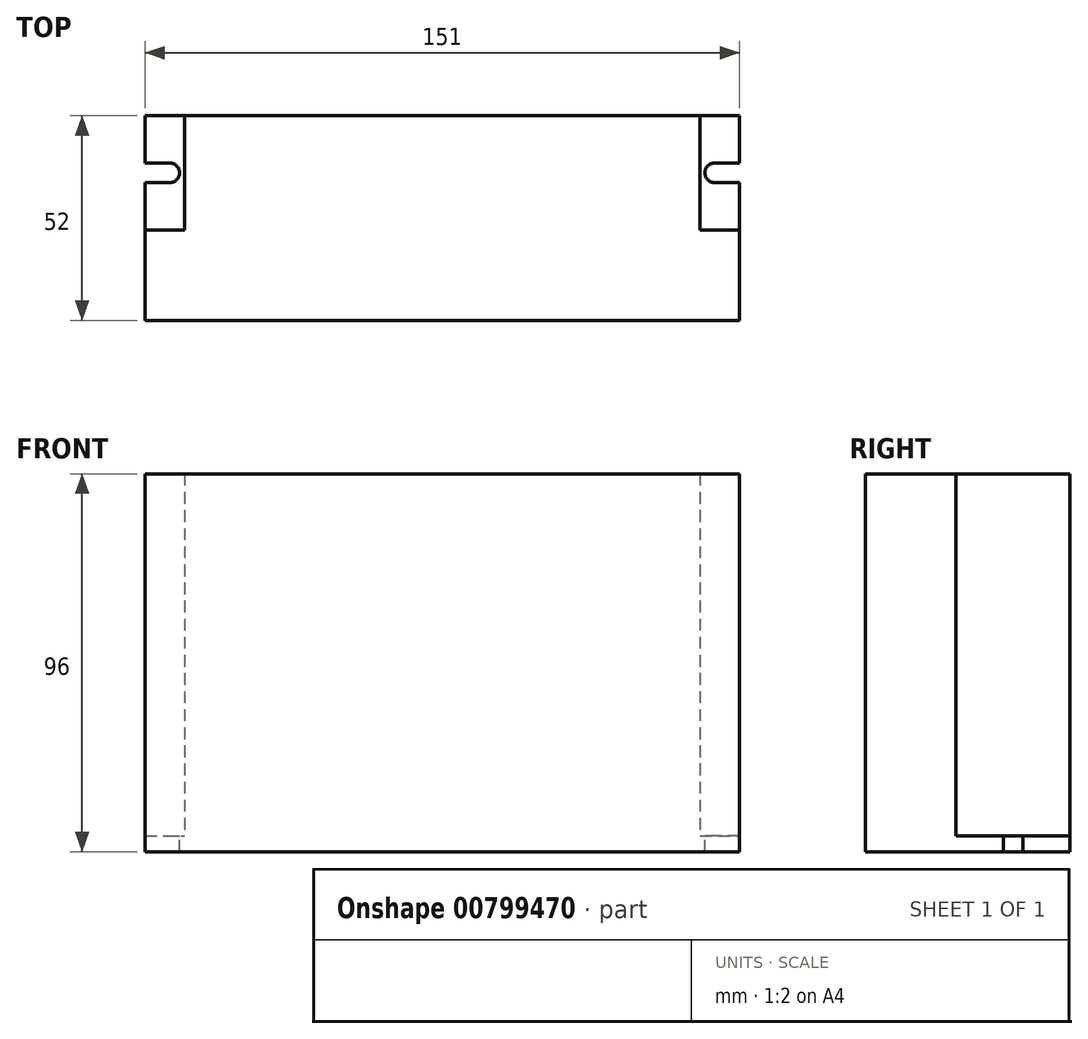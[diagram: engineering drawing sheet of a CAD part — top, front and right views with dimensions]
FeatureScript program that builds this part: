
annotation { "Feature Type Name" : "Feature", "Feature Type Description" : "" }
export const myFeature = defineFeature(function(context is Context, id is Id, definition is map)
    precondition{}
    {
        {
            var Q0;
            Q0=qCreatedBy(makeId("Top.planeOp"),FACE);
            var sketch = newSketch(context, id + "F0", { "sketchPlane" : qUnion([Q0])});
            skLineSegment(sketch, "E0.bottom", {"start": v(0, 0) * mm, "end": v(151, 0) * mm});
            skLineSegment(sketch, "E0.top", {"start": v(0, 52) * mm, "end": v(151, 52) * mm});
            skLineSegment(sketch, "E0.left", {"start": v(0, 0) * mm, "end": v(0, 52) * mm});
            skLineSegment(sketch, "E0.right", {"start": v(151, 0) * mm, "end": v(151, 52) * mm});
            skSolve(sketch);
        }
        {
            var Q0;
            Q0=makeQuery(id+"F0.imprint","IMPRINT",FACE,{"disambiguationData":[TD([[makeQuery(id+"F0.imprint","IMPRINT",EDGE,{"derivedFrom":sQuery(id+"F0.wireOp",EDGE,"E0.bottom")}),1.0]])]});
            extrude(context, id + "F1", {"entities" : qUnion([Q0]), "depth" : 4 * mm, "offsetDistance" : 25 * mm});
        }
        {
            var Q0;
            Q0=makeQuery(id+"F1.opExtrude","CAP_FACE",FACE,{"disambiguationData":[OSD([sQuery(id+"F0.wireOp",EDGE,"E0.bottom"),sQuery(id+"F0.wireOp",EDGE,"E0.top"),sQuery(id+"F0.wireOp",EDGE,"E0.left"),sQuery(id+"F0.wireOp",EDGE,"E0.right")])],"isStart":false});
            var sketch = newSketch(context, id + "F2", { "sketchPlane" : qUnion([Q0])});
            skLineSegment(sketch, "E1.bottom", {"start": v(151, 52) * mm, "end": v(141, 52) * mm});
            skLineSegment(sketch, "E1.top", {"start": v(151, 23) * mm, "end": v(141, 23) * mm});
            skLineSegment(sketch, "E1.left", {"start": v(151, 52) * mm, "end": v(151, 23) * mm});
            skLineSegment(sketch, "E1.right", {"start": v(141, 52) * mm, "end": v(141, 23) * mm});
            skLineSegment(sketch, "E2.bottom", {"start": v(0, 52) * mm, "end": v(10, 52) * mm});
            skLineSegment(sketch, "E2.top", {"start": v(0, 23) * mm, "end": v(10, 23) * mm});
            skLineSegment(sketch, "E2.left", {"start": v(0, 52) * mm, "end": v(0, 23) * mm});
            skLineSegment(sketch, "E2.right", {"start": v(10, 52) * mm, "end": v(10, 23) * mm});
            skArc(sketch, "E3", {"start": v(6.26, 35) * mm, "mid": v(8.76, 37.5) * mm, "end": v(6.26, 40) * mm});
            skPoint(sketch, "E3.centerSnap0", {"position": v(10, 37.5) * mm});
            skLineSegment(sketch, "E4", {"start": v(0, 40) * mm, "end": v(6.26, 40) * mm});
            skLineSegment(sketch, "E5", {"start": v(6.26, 35) * mm, "end": v(0, 35) * mm});
            skLineSegment(sketch, "E6", {"start": v(75.5, 52) * mm, "end": v(75.5, 0) * mm});
            skLineSegment(sketch, "E7.MirrorCS", {"start": v(151, 40) * mm, "end": v(144.74, 40) * mm});
            skLineSegment(sketch, "E8.MirrorCS", {"start": v(144.74, 35) * mm, "end": v(151, 35) * mm});
            skArc(sketch, "E9.MirrorCS", {"start": v(144.74, 35) * mm, "mid": v(142.24, 37.5) * mm, "end": v(144.74, 40) * mm});
            skSolve(sketch);
        }
        {
            var Q0;
            {var subQ3=sQuery(id+"F2.wireOp",EDGE,"E1.top");Q0=makeQuery(id+"F2.imprint","IMPRINT",FACE,{"disambiguationData":[TD([[makeQuery(id+"F2.imprint","IMPRINT",EDGE,{"derivedFrom":subQ3}),1.0]])]});}
            var Q1;
            {var subQ3=sQuery(id+"F2.wireOp",EDGE,"E2.top");Q1=makeQuery(id+"F2.imprint","IMPRINT",FACE,{"disambiguationData":[TD([[makeQuery(id+"F2.imprint","IMPRINT",EDGE,{"derivedFrom":subQ3}),-1.0]])]});}
            extrude(context, id + "F3", {"entities" : qUnion([Q0, Q1]), "operationType" : NewBodyOperationType.ADD, "depth" : 92 * mm, "offsetDistance" : 25 * mm});
        }
        {
            var Q0;
            Q0=makeQuery(id+"F2.imprint","IMPRINT",FACE,{"disambiguationData":[TD([[makeQuery(id+"F2.imprint","IMPRINT",EDGE,{"derivedFrom":sQuery(id+"F2.wireOp",EDGE,"E3")}),1.0]])]});
            var Q1;
            {var subQ0=sQuery(id+"F2.wireOp",EDGE,"E7.MirrorCS");Q1=makeQuery(id+"F2.imprint","IMPRINT",FACE,{"disambiguationData":[TD([[makeQuery(id+"F2.imprint","IMPRINT",EDGE,{"derivedFrom":subQ0}),1.0]])]});}
            extrude(context, id + "F4", {"entities" : qUnion([Q0, Q1]), "operationType" : NewBodyOperationType.REMOVE, "oppositeDirection" : true, "depth" : 25 * mm, "offsetDistance" : 25 * mm});
        }
    });
